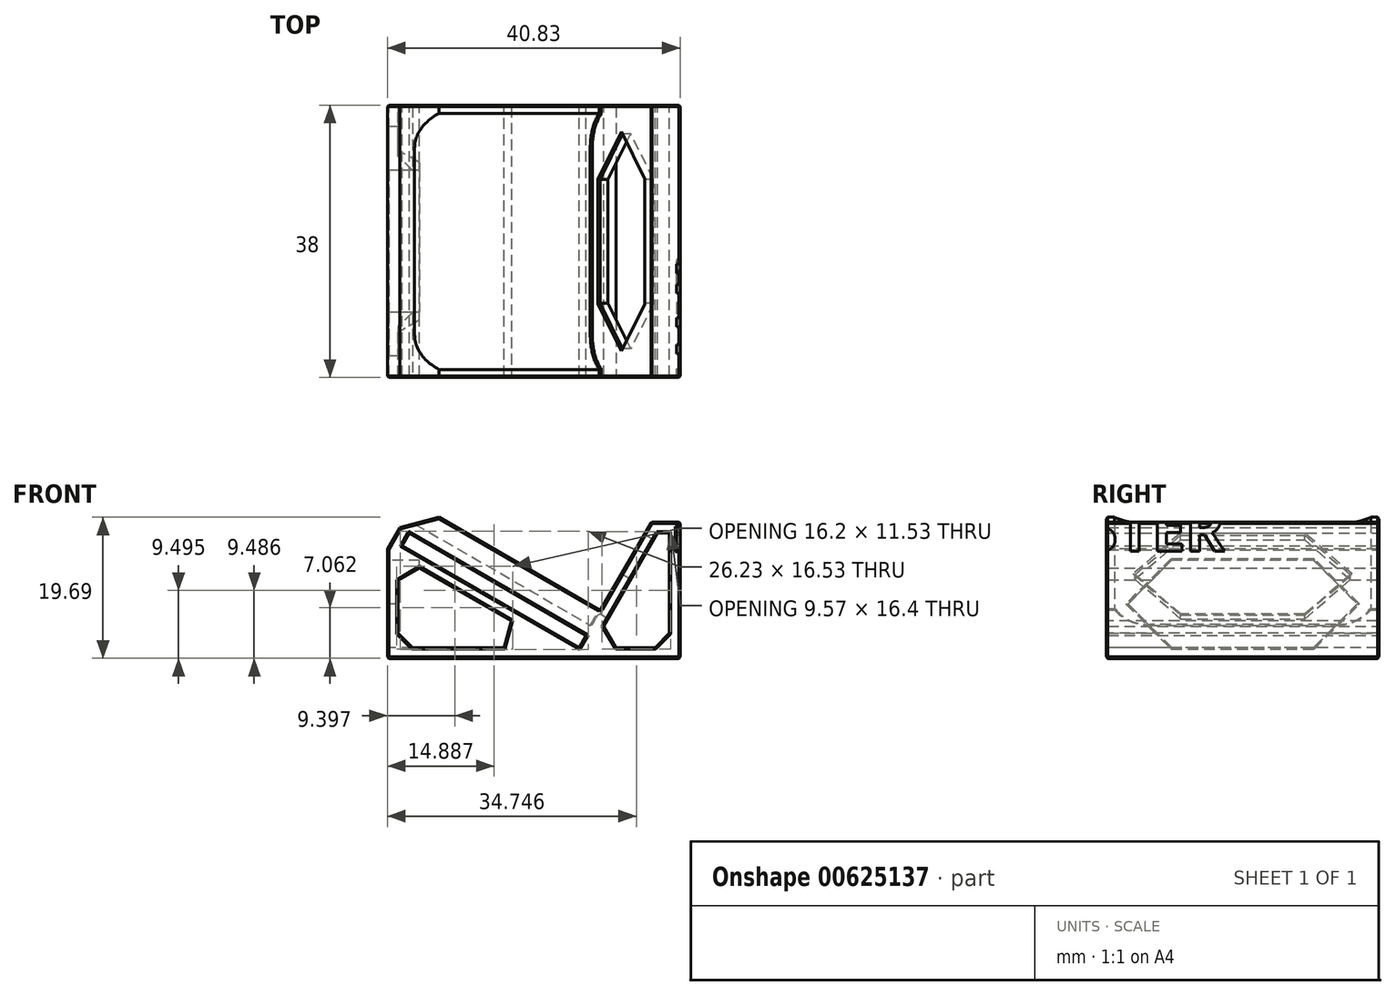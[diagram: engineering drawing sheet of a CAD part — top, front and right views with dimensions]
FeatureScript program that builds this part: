
annotation { "Feature Type Name" : "Feature", "Feature Type Description" : "" }
export const myFeature = defineFeature(function(context is Context, id is Id, definition is map)
    precondition{}
    {
        {
            var Q0;
            Q0=qCreatedBy(makeId("Front.planeOp"),FACE);
            var sketch = newSketch(context, id + "F0", { "sketchPlane" : qUnion([Q0])});
            skLineSegment(sketch, "E0", {"start": v(19.56, -9.2) * mm, "end": v(19.56, 9.8) * mm});
            skLineSegment(sketch, "E1", {"start": v(15.56, 9.8) * mm, "end": v(7.2, -4.67) * mm});
            skLineSegment(sketch, "E2", {"start": v(7.2, -4.67) * mm, "end": v(-18.77, 10.33) * mm});
            skLineSegment(sketch, "E3", {"start": v(2.46, -7.7) * mm, "end": v(-19.77, 5.13) * mm});
            skPoint(sketch, "E4", {"position": v(0, 0) * mm});
            skLineSegment(sketch, "E5", {"start": v(-18.22, 8.28) * mm, "end": v(6.46, -5.97) * mm});
            skLineSegment(sketch, "E6", {"start": v(6.46, -5.97) * mm, "end": v(5.46, -7.7) * mm});
            skLineSegment(sketch, "E7", {"start": v(19.56, 9.8) * mm, "end": v(15.56, 9.8) * mm});
            skLineSegment(sketch, "E8", {"start": v(7.19, -7.7) * mm, "end": v(16.43, 8.3) * mm});
            skLineSegment(sketch, "E9", {"start": v(16.43, 8.3) * mm, "end": v(18.06, 8.3) * mm});
            skLineSegment(sketch, "E10", {"start": v(18.06, 8.3) * mm, "end": v(18.06, -7.7) * mm});
            skLineSegment(sketch, "E11", {"start": v(18.06, -7.7) * mm, "end": v(7.19, -7.7) * mm});
            skLineSegment(sketch, "E12", {"start": v(5.46, -7.7) * mm, "end": v(-19.22, 6.55) * mm});
            skLineSegment(sketch, "E13", {"start": v(-18.22, 8.28) * mm, "end": v(-19.22, 6.55) * mm});
            skLineSegment(sketch, "E14", {"start": v(-18.77, 10.33) * mm, "end": v(-21.27, 6) * mm});
            skLineSegment(sketch, "E15", {"start": v(-21.27, 6) * mm, "end": v(-21.27, -9.2) * mm});
            skLineSegment(sketch, "E16", {"start": v(-21.27, -9.2) * mm, "end": v(19.56, -9.2) * mm});
            skLineSegment(sketch, "E17.0", {"start": v(-19.77, -7.7) * mm, "end": v(2.46, -7.7) * mm});
            skLineSegment(sketch, "E17.1", {"start": v(-19.77, 5.13) * mm, "end": v(-19.77, -7.7) * mm});
            skSolve(sketch);
        }
        {
            var Q0;
            {var subQ3=sQuery(id+"F0.wireOp",EDGE,"E2");Q0=makeQuery(id+"F0.imprint","IMPRINT",FACE,{"disambiguationData":[TD([[makeQuery(id+"F0.imprint","IMPRINT",EDGE,{"derivedFrom":subQ3}),1.0]])]});}
            extrude(context, id + "F1", {"entities" : qUnion([Q0]), "endBound" : BoundingType.SYMMETRIC, "depth" : 38 * mm, "offsetDistance" : 25 * mm});
        }
        {
            var Q0;
            Q0=makeQuery(id+"F1.opExtrude","SWEPT_FACE",FACE,{"disambiguationData":[OSD([sQuery(id+"F0.wireOp",EDGE,"E0")])]});
            var sketch = newSketch(context, id + "F2", { "sketchPlane" : qUnion([Q0])});
            skText(sketch, "E18", { "text": "AIRSTER", "fontName": "OpenSans-Bold.ttf"});
            skPoint(sketch, "E19", {"position": v(-17, 0.3) * mm});
            skPoint(sketch, "E20", {"position": v(-19, 0.3) * mm});
            skPoint(sketch, "E21", {"position": v(0, 9.8) * mm});
            const initialGuessF2  = {"E18": [-0.036, 0.00576, 1, 0, 0.00598]};
            skSetInitialGuess(sketch, initialGuessF2);
            skSolve(sketch);
        }
        {
            var Q0;
            Q0=qSketchRegion(id+"F2",true);
            extrude(context, id + "F3", {"entities" : qUnion([Q0]), "operationType" : NewBodyOperationType.REMOVE, "oppositeDirection" : true, "depth" : 0.5 * mm});
        }
        {
            var Q0;
            Q0=makeQuery(id+"F1.opExtrude","SWEPT_EDGE",EDGE,{"disambiguationData":[OSD([sQuery(id+"F0.wireOp",EDGE,"E8"),sQuery(id+"F0.wireOp",EDGE,"E11")])]});
            var Q1;
            Q1=makeQuery(id+"F1.opExtrude","SWEPT_EDGE",EDGE,{"disambiguationData":[OSD([sQuery(id+"F0.wireOp",EDGE,"E10"),sQuery(id+"F0.wireOp",EDGE,"E11")])]});
            var Q2;
            Q2=makeQuery(id+"F1.opExtrude","SWEPT_EDGE",EDGE,{"disambiguationData":[OSD([sQuery(id+"F0.wireOp",EDGE,"E17.0"),sQuery(id+"F0.wireOp",EDGE,"E17.1")])]});
            var Q3;
            Q3=makeQuery(id+"F1.opExtrude","SWEPT_EDGE",EDGE,{"disambiguationData":[OSD([sQuery(id+"F0.wireOp",EDGE,"E3"),sQuery(id+"F0.wireOp",EDGE,"E17.1")])]});
            chamfer(context, id + "F4", {"entities" : qUnion([Q0, Q1, Q2, Q3]), "width" : 2 * mm, "tangentPropagation" : true});
        }
        {
            var Q0;
            Q0=makeQuery(id+"F1.opExtrude","SWEPT_FACE",FACE,{"disambiguationData":[OSD([sQuery(id+"F0.wireOp",EDGE,"E1")])]});
            var sketch = newSketch(context, id + "F5", { "sketchPlane" : qUnion([Q0])});
            skArc(sketch, "E22", {"start": v(-19, 5.56) * mm, "mid": v(-17.24, 1.31) * mm, "end": v(-13, -0.44) * mm});
            skArc(sketch, "E23.MirrorCS", {"start": v(19, 5.56) * mm, "mid": v(17.24, 1.31) * mm, "end": v(13, -0.44) * mm});
            skLineSegment(sketch, "E24", {"start": v(-19, 2.06) * mm, "end": v(-17.87, 2.06) * mm});
            skLineSegment(sketch, "E25.MirrorCS", {"start": v(19, 2.06) * mm, "end": v(17.87, 2.06) * mm});
            skLineSegment(sketch, "E26", {"start": v(0, 14.26) * mm, "end": v(-15, 14.26) * mm});
            skLineSegment(sketch, "E27", {"start": v(-15, 14.26) * mm, "end": v(-15, 1.56) * mm});
            skLineSegment(sketch, "E28", {"start": v(-15, 1.56) * mm, "end": v(0, 1.56) * mm});
            skLineSegment(sketch, "E29.MirrorCS", {"start": v(0, 14.26) * mm, "end": v(15, 14.26) * mm});
            skLineSegment(sketch, "E30.MirrorCS", {"start": v(15, 14.26) * mm, "end": v(15, 1.56) * mm});
            skLineSegment(sketch, "E31.MirrorCS", {"start": v(15, 1.56) * mm, "end": v(0, 1.56) * mm});
            skPoint(sketch, "E32", {"position": v(-15, 7.91) * mm});
            skLineSegment(sketch, "E33", {"start": v(-15, 7.91) * mm, "end": v(-8.65, 14.26) * mm});
            skLineSegment(sketch, "E34", {"start": v(-15, 7.91) * mm, "end": v(-8.65, 1.56) * mm});
            skLineSegment(sketch, "E35.MirrorCS", {"start": v(15, 7.91) * mm, "end": v(8.65, 14.26) * mm});
            skLineSegment(sketch, "E36.MirrorCS", {"start": v(15, 7.91) * mm, "end": v(8.65, 1.56) * mm});
            skSolve(sketch);
        }
        {
            var Q0;
            {var subQ4=sQuery(id+"F5.wireOp",EDGE,"E24");Q0=makeQuery(id+"F5.imprint","IMPRINT",FACE,{"disambiguationData":[TD([[makeQuery(id+"F5.imprint","IMPRINT",EDGE,{"derivedFrom":subQ4}),-1.0]])]});}
            var Q1;
            {var subQ4=sQuery(id+"F5.wireOp",EDGE,"E25.MirrorCS");Q1=makeQuery(id+"F5.imprint","IMPRINT",FACE,{"disambiguationData":[TD([[makeQuery(id+"F5.imprint","IMPRINT",EDGE,{"derivedFrom":subQ4}),1.0]])]});}
            var Q2;
            Q2=makeQuery(id+"F1.opExtrude","SWEPT_FACE",FACE,{"disambiguationData":[OSD([sQuery(id+"F0.wireOp",EDGE,"E14")])]});
            extrude(context, id + "F6", {"entities" : qUnion([Q0, Q1]), "operationType" : NewBodyOperationType.ADD, "endBound" : BoundingType.UP_TO_SURFACE, "depth" : 25 * mm, "endBoundEntityFace" : qUnion([Q2]), "offsetDistance" : 25 * mm});
        }
        {
            var Q0;
            Q0=makeQuery(id+"F6.opExtrude","CAP_EDGE",EDGE,{"disambiguationData":[OSD([sQuery(id+"F5.wireOp",EDGE,"E24")])],"isStart":false});
            var Q1;
            Q1=makeQuery(id+"F6.opExtrude","CAP_EDGE",EDGE,{"disambiguationData":[OSD([sQuery(id+"F5.wireOp",EDGE,"E25.MirrorCS")])],"isStart":false});
            chamfer(context, id + "F7", {"entities" : qUnion([Q0, Q1]), "width" : 4 * mm, "tangentPropagation" : true});
        }
        {
            var Q0;
            {var subQ7=sQuery(id+"F5.wireOp",EDGE,"E33");Q0=makeQuery(id+"F5.imprint","IMPRINT",FACE,{"disambiguationData":[TD([[makeQuery(id+"F5.imprint","IMPRINT",EDGE,{"derivedFrom":subQ7}),-1.0]])]});}
            var Q1;
            Q1=makeQuery(id+"F1.opExtrude","SWEPT_FACE",FACE,{"disambiguationData":[OSD([sQuery(id+"F0.wireOp",EDGE,"E8")])]});
            extrude(context, id + "F8", {"entities" : qUnion([Q0]), "operationType" : NewBodyOperationType.REMOVE, "endBound" : BoundingType.UP_TO_SURFACE, "oppositeDirection" : true, "depth" : 25 * mm, "endBoundEntityFace" : qUnion([Q1]), "offsetDistance" : 25 * mm});
        }
        {
            var Q0;
            Q0=makeQuery(id+"F1.opExtrude","SWEPT_FACE",FACE,{"disambiguationData":[OSD([sQuery(id+"F0.wireOp",EDGE,"E15")])]});
            var sketch = newSketch(context, id + "F9", { "sketchPlane" : qUnion([Q0])});
            skLineSegment(sketch, "E37", {"start": v(0, 4.5) * mm, "end": v(-16, 4.5) * mm});
            skLineSegment(sketch, "E38", {"start": v(-16, 4.5) * mm, "end": v(-16, -7.7) * mm});
            skLineSegment(sketch, "E39", {"start": v(-16, -7.7) * mm, "end": v(0, -7.7) * mm});
            skPoint(sketch, "E40", {"position": v(-16, -1.6) * mm});
            skLineSegment(sketch, "E41", {"start": v(-16, -1.6) * mm, "end": v(-9.9, 4.5) * mm});
            skLineSegment(sketch, "E42", {"start": v(-16, -1.6) * mm, "end": v(-9.9, -7.7) * mm});
            skLineSegment(sketch, "E43.MirrorCS", {"start": v(0, 4.5) * mm, "end": v(16, 4.5) * mm});
            skLineSegment(sketch, "E44.MirrorCS", {"start": v(16, -1.6) * mm, "end": v(9.9, 4.5) * mm});
            skLineSegment(sketch, "E45.MirrorCS", {"start": v(16, -1.6) * mm, "end": v(9.9, -7.7) * mm});
            skLineSegment(sketch, "E46.MirrorCS", {"start": v(16, -7.7) * mm, "end": v(0, -7.7) * mm});
            skLineSegment(sketch, "E47.MirrorCS", {"start": v(16, 4.5) * mm, "end": v(16, -7.7) * mm});
            skSolve(sketch);
        }
        {
            var Q0;
            {var subQ1=sQuery(id+"F9.wireOp",EDGE,"E41");Q0=makeQuery(id+"F9.imprint","IMPRINT",FACE,{"disambiguationData":[TD([[makeQuery(id+"F9.imprint","IMPRINT",EDGE,{"derivedFrom":subQ1}),-1.0]])]});}
            var Q1;
            {var subQ0=sQuery(id+"F0.wireOp",EDGE,"E3");var subQ1=sQuery(id+"F0.wireOp",EDGE,"E17.1");Q1=makeQuery(id+"F4.opChamfer","BLEND_VERTEX",VERTEX,{"blendedFrom":[makeQuery(id+"F1.opExtrude","SWEPT_EDGE",EDGE,{"disambiguationData":[OSD([subQ0,subQ1])]}),makeQuery(id+"F1.opExtrude","CAP_FACE",FACE,{"disambiguationData":[OSD([sQuery(id+"F0.wireOp",EDGE,"E0"),sQuery(id+"F0.wireOp",EDGE,"E1"),sQuery(id+"F0.wireOp",EDGE,"E2"),subQ0,sQuery(id+"F0.wireOp",EDGE,"E5"),sQuery(id+"F0.wireOp",EDGE,"E6"),sQuery(id+"F0.wireOp",EDGE,"E7"),sQuery(id+"F0.wireOp",EDGE,"E8"),sQuery(id+"F0.wireOp",EDGE,"E9"),sQuery(id+"F0.wireOp",EDGE,"E10"),sQuery(id+"F0.wireOp",EDGE,"E11"),sQuery(id+"F0.wireOp",EDGE,"E12"),sQuery(id+"F0.wireOp",EDGE,"E13"),sQuery(id+"F0.wireOp",EDGE,"E14"),sQuery(id+"F0.wireOp",EDGE,"E15"),sQuery(id+"F0.wireOp",EDGE,"E16"),sQuery(id+"F0.wireOp",EDGE,"E17.0"),subQ1])],"isStart":true}),makeQuery(id+"F1.opExtrude","SWEPT_FACE",FACE,{"disambiguationData":[OSD([subQ0])]})],"blendedInto":[makeQuery(id+"F1.opExtrude","CAP_FACE",FACE,{"disambiguationData":[OSD([sQuery(id+"F0.wireOp",EDGE,"E0"),sQuery(id+"F0.wireOp",EDGE,"E1"),sQuery(id+"F0.wireOp",EDGE,"E2"),subQ0,sQuery(id+"F0.wireOp",EDGE,"E5"),sQuery(id+"F0.wireOp",EDGE,"E6"),sQuery(id+"F0.wireOp",EDGE,"E7"),sQuery(id+"F0.wireOp",EDGE,"E8"),sQuery(id+"F0.wireOp",EDGE,"E9"),sQuery(id+"F0.wireOp",EDGE,"E10"),sQuery(id+"F0.wireOp",EDGE,"E11"),sQuery(id+"F0.wireOp",EDGE,"E12"),sQuery(id+"F0.wireOp",EDGE,"E13"),sQuery(id+"F0.wireOp",EDGE,"E14"),sQuery(id+"F0.wireOp",EDGE,"E15"),sQuery(id+"F0.wireOp",EDGE,"E16"),sQuery(id+"F0.wireOp",EDGE,"E17.0"),subQ1])],"isStart":true}),makeQuery(id+"F1.opExtrude","SWEPT_FACE",FACE,{"disambiguationData":[OSD([subQ0])]})]});}
            extrude(context, id + "F10", {"entities" : qUnion([Q0]), "operationType" : NewBodyOperationType.REMOVE, "endBound" : BoundingType.UP_TO_VERTEX, "oppositeDirection" : true, "depth" : 25 * mm, "endBoundEntityVertex" : qUnion([Q1]), "offsetDistance" : 25 * mm});
        }
        {
            var Q0;
            Q0=makeQuery(id+"F1.opExtrude","SWEPT_EDGE",EDGE,{"disambiguationData":[OSD([sQuery(id+"F0.wireOp",EDGE,"E3"),sQuery(id+"F0.wireOp",EDGE,"E17.0")])]});
            chamfer(context, id + "F11", {"entities" : qUnion([Q0]), "width" : 2 * mm, "tangentPropagation" : true});
        }
        {
            var Q0;
            {var subQ0=sQuery(id+"F0.wireOp",EDGE,"E1");var subQ1=makeQuery(id+"F1.opExtrude","CAP_EDGE",EDGE,{"disambiguationData":[OSD([subQ0])],"isStart":false});var subQ2=sQuery(id+"F0.wireOp",EDGE,"E2");Q0=makeQuery(id+"F6.boolean.opBoolean","MERGE",FACE,{"derivedFrom":[makeQuery(id+"F1.opExtrude","CAP_FACE",FACE,{"disambiguationData":[OSD([sQuery(id+"F0.wireOp",EDGE,"E0"),subQ0,subQ2,sQuery(id+"F0.wireOp",EDGE,"E3"),sQuery(id+"F0.wireOp",EDGE,"E5"),sQuery(id+"F0.wireOp",EDGE,"E6"),sQuery(id+"F0.wireOp",EDGE,"E7"),sQuery(id+"F0.wireOp",EDGE,"E8"),sQuery(id+"F0.wireOp",EDGE,"E9"),sQuery(id+"F0.wireOp",EDGE,"E10"),sQuery(id+"F0.wireOp",EDGE,"E11"),sQuery(id+"F0.wireOp",EDGE,"E12"),sQuery(id+"F0.wireOp",EDGE,"E13"),sQuery(id+"F0.wireOp",EDGE,"E14"),sQuery(id+"F0.wireOp",EDGE,"E15"),sQuery(id+"F0.wireOp",EDGE,"E16"),sQuery(id+"F0.wireOp",EDGE,"E17.0"),sQuery(id+"F0.wireOp",EDGE,"E17.1")])],"isStart":false}),makeQuery(id+"F6.opExtrude","SWEPT_FACE",FACE,{"disambiguationData":[OSD([subQ0]),TDD([makeQuery(id+"F5.imprint","IMPRINT",EDGE,{"disambiguationData":[TD([[makeQuery(id+"F5.imprint","INTERSECT",VERTEX,{"derivedFrom":[subQ1,sQuery(id+"F5.wireOp",EDGE,"E25.MirrorCS")]}),-1.0]])],"derivedFrom":subQ1})])]})]});}
            var Q1;
            Q1=makeQuery(id+"F1.opExtrude","SWEPT_FACE",FACE,{"disambiguationData":[OSD([sQuery(id+"F0.wireOp",EDGE,"E15")])]});
            var Q2;
            Q2=makeQuery(id+"F1.opExtrude","SWEPT_FACE",FACE,{"disambiguationData":[OSD([sQuery(id+"F0.wireOp",EDGE,"E1")])]});
            var Q3;
            Q3=makeQuery(id+"F1.opExtrude","SWEPT_EDGE",EDGE,{"disambiguationData":[OSD([sQuery(id+"F0.wireOp",EDGE,"E0"),sQuery(id+"F0.wireOp",EDGE,"E7")])]});
            var Q4;
            Q4=makeQuery(id+"F1.opExtrude","SWEPT_EDGE",EDGE,{"disambiguationData":[OSD([sQuery(id+"F0.wireOp",EDGE,"E0"),sQuery(id+"F0.wireOp",EDGE,"E16")])]});
            var Q5;
            {var subQ0=sQuery(id+"F0.wireOp",EDGE,"E1");var subQ1=makeQuery(id+"F1.opExtrude","CAP_EDGE",EDGE,{"disambiguationData":[OSD([subQ0])],"isStart":true});var subQ2=sQuery(id+"F0.wireOp",EDGE,"E2");Q5=makeQuery(id+"F6.boolean.opBoolean","MERGE",FACE,{"derivedFrom":[makeQuery(id+"F1.opExtrude","CAP_FACE",FACE,{"disambiguationData":[OSD([sQuery(id+"F0.wireOp",EDGE,"E0"),subQ0,subQ2,sQuery(id+"F0.wireOp",EDGE,"E3"),sQuery(id+"F0.wireOp",EDGE,"E5"),sQuery(id+"F0.wireOp",EDGE,"E6"),sQuery(id+"F0.wireOp",EDGE,"E7"),sQuery(id+"F0.wireOp",EDGE,"E8"),sQuery(id+"F0.wireOp",EDGE,"E9"),sQuery(id+"F0.wireOp",EDGE,"E10"),sQuery(id+"F0.wireOp",EDGE,"E11"),sQuery(id+"F0.wireOp",EDGE,"E12"),sQuery(id+"F0.wireOp",EDGE,"E13"),sQuery(id+"F0.wireOp",EDGE,"E14"),sQuery(id+"F0.wireOp",EDGE,"E15"),sQuery(id+"F0.wireOp",EDGE,"E16"),sQuery(id+"F0.wireOp",EDGE,"E17.0"),sQuery(id+"F0.wireOp",EDGE,"E17.1")])],"isStart":true}),makeQuery(id+"F6.opExtrude","SWEPT_FACE",FACE,{"disambiguationData":[OSD([subQ0]),TDD([makeQuery(id+"F5.imprint","IMPRINT",EDGE,{"disambiguationData":[TD([[makeQuery(id+"F5.imprint","INTERSECT",VERTEX,{"derivedFrom":[subQ1,sQuery(id+"F5.wireOp",EDGE,"E24")]}),-1.0]])],"derivedFrom":subQ1})])]})]});}
            chamfer(context, id + "F12", {"entities" : qUnion([Q0, Q1, Q2, Q3, Q4, Q5]), "width" : 0.2 * mm, "tangentPropagation" : true});
        }
    });
